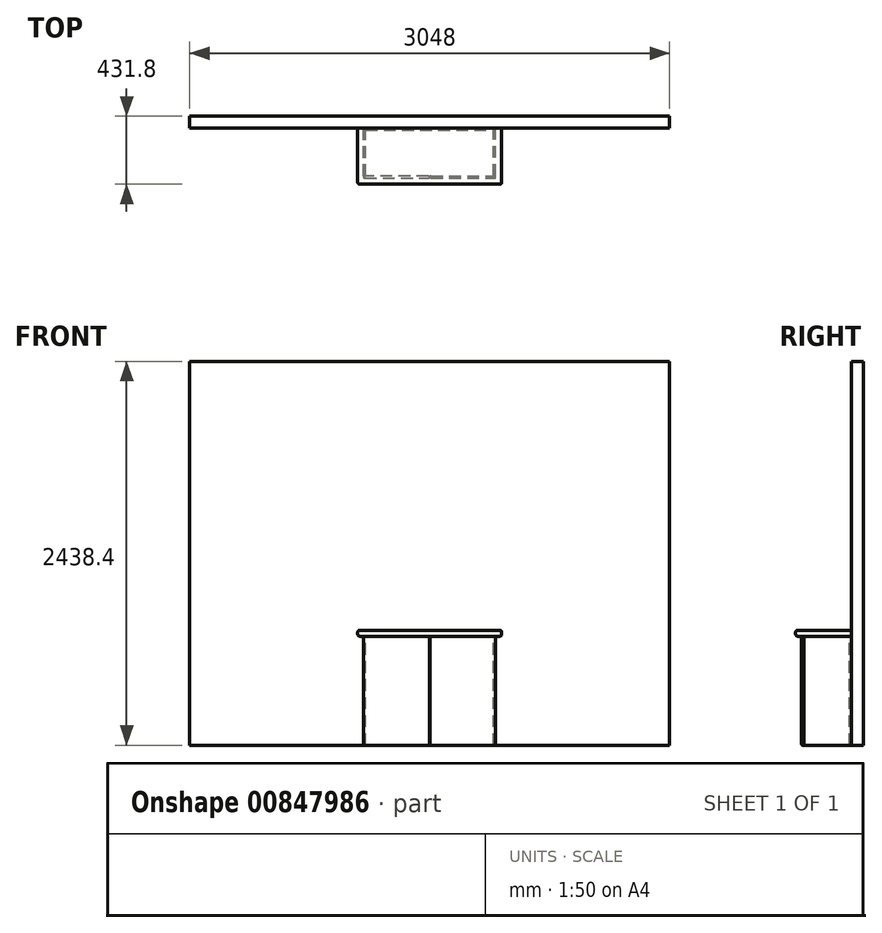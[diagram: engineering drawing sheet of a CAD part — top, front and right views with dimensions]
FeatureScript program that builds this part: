
annotation { "Feature Type Name" : "Feature", "Feature Type Description" : "" }
export const myFeature = defineFeature(function(context is Context, id is Id, definition is map)
    precondition{}
    {
        {
            var Q0;
            Q0=qCreatedBy(makeId("Front.planeOp"),FACE);
            var sketch = newSketch(context, id + "F0", { "sketchPlane" : qUnion([Q0])});
            skLineSegment(sketch, "E0.bottom", {"start": v(1524, -1219.2) * mm, "end": v(-1524, -1219.2) * mm});
            skLineSegment(sketch, "E0.top", {"start": v(1524, 1219.2) * mm, "end": v(-1524, 1219.2) * mm});
            skLineSegment(sketch, "E0.left", {"start": v(1524, -1219.2) * mm, "end": v(1524, 1219.2) * mm});
            skLineSegment(sketch, "E0.right", {"start": v(-1524, -1219.2) * mm, "end": v(-1524, 1219.2) * mm});
            skPoint(sketch, "E0.middle", {"position": v(0, 0) * mm});
            skSolve(sketch);
        }
        {
            var Q0;
            Q0=makeQuery(id+"F0.imprint","IMPRINT",FACE,{"disambiguationData":[TD([[makeQuery(id+"F0.imprint","IMPRINT",EDGE,{"derivedFrom":sQuery(id+"F0.wireOp",EDGE,"E0.bottom")}),-1.0]])]});
            extrude(context, id + "F1", {"entities" : qUnion([Q0]), "depth" : 76.2 * mm, "offsetDistance" : 25.4 * mm});
        }
        {
            var Q0;
            Q0=makeQuery(id+"F1.opExtrude","CAP_FACE",FACE,{"disambiguationData":[OSD([sQuery(id+"F0.wireOp",EDGE,"E0.bottom"),sQuery(id+"F0.wireOp",EDGE,"E0.top"),sQuery(id+"F0.wireOp",EDGE,"E0.left"),sQuery(id+"F0.wireOp",EDGE,"E0.right")])],"isStart":false});
            var sketch = newSketch(context, id + "F2", { "sketchPlane" : qUnion([Q0])});
            skLineSegment(sketch, "E1", {"start": v(0, 1219.2) * mm, "end": v(0, -1219.2) * mm, "construction": true});
            skLineSegment(sketch, "E2", {"start": v(1524, -508) * mm, "end": v(-1524, -508) * mm, "construction": true});
            skLineSegment(sketch, "E3.bottom", {"start": v(457.2, -488.95) * mm, "end": v(-457.2, -488.95) * mm});
            skLineSegment(sketch, "E3.top", {"start": v(457.2, -527.05) * mm, "end": v(-457.2, -527.05) * mm});
            skLineSegment(sketch, "E3.left", {"start": v(457.2, -488.95) * mm, "end": v(457.2, -527.05) * mm});
            skLineSegment(sketch, "E3.right", {"start": v(-457.2, -488.95) * mm, "end": v(-457.2, -527.05) * mm});
            skPoint(sketch, "E3.middle", {"position": v(0, -508) * mm});
            skSolve(sketch);
        }
        {
            var Q0;
            Q0=makeQuery(id+"F2.imprint","IMPRINT",FACE,{"disambiguationData":[TD([[makeQuery(id+"F2.imprint","IMPRINT",EDGE,{"derivedFrom":sQuery(id+"F2.wireOp",EDGE,"E3.bottom")}),1.0]])]});
            extrude(context, id + "F3", {"entities" : qUnion([Q0]), "depth" : 355.6 * mm, "offsetDistance" : 25.4 * mm});
        }
        {
            var Q0;
            Q0=makeQuery(id+"F3.opExtrude","CAP_EDGE",EDGE,{"disambiguationData":[OSD([sQuery(id+"F2.wireOp",EDGE,"E3.left")])],"isStart":false});
            var Q1;
            Q1=makeQuery(id+"F3.opExtrude","CAP_EDGE",EDGE,{"disambiguationData":[OSD([sQuery(id+"F2.wireOp",EDGE,"E3.right")])],"isStart":false});
            fillet(context, id + "F4", {"entities" : qUnion([Q0, Q1]), "radius" : 12.7 * mm, "tangentPropagation" : true, "allowEdgeOverflow" : false});
        }
        {
            var Q0;
            Q0=makeQuery(id+"F3.opExtrude","SWEPT_EDGE",EDGE,{"disambiguationData":[OSD([sQuery(id+"F2.wireOp",EDGE,"E3.bottom"),sQuery(id+"F2.wireOp",EDGE,"E3.left")])]});
            var Q1;
            Q1=makeQuery(id+"F3.opExtrude","SWEPT_EDGE",EDGE,{"disambiguationData":[OSD([sQuery(id+"F2.wireOp",EDGE,"E3.top"),sQuery(id+"F2.wireOp",EDGE,"E3.left")])]});
            var Q2;
            Q2=makeQuery(id+"F3.opExtrude","CAP_EDGE",EDGE,{"disambiguationData":[OSD([sQuery(id+"F2.wireOp",EDGE,"E3.bottom")])],"isStart":false});
            var Q3;
            Q3=makeQuery(id+"F3.opExtrude","CAP_EDGE",EDGE,{"disambiguationData":[OSD([sQuery(id+"F2.wireOp",EDGE,"E3.top")])],"isStart":false});
            var Q4;
            Q4=makeQuery(id+"F3.opExtrude","SWEPT_EDGE",EDGE,{"disambiguationData":[OSD([sQuery(id+"F2.wireOp",EDGE,"E3.bottom"),sQuery(id+"F2.wireOp",EDGE,"E3.right")])]});
            var Q5;
            Q5=makeQuery(id+"F3.opExtrude","SWEPT_EDGE",EDGE,{"disambiguationData":[OSD([sQuery(id+"F2.wireOp",EDGE,"E3.top"),sQuery(id+"F2.wireOp",EDGE,"E3.right")])]});
            fillet(context, id + "F5", {"entities" : qUnion([Q0, Q1, Q2, Q3, Q4, Q5]), "radius" : 12.7 * mm, "tangentPropagation" : true, "allowEdgeOverflow" : false});
        }
        {
            var Q0;
            Q0=makeQuery(id+"F3.opExtrude","SWEPT_FACE",FACE,{"disambiguationData":[OSD([sQuery(id+"F2.wireOp",EDGE,"E3.top")])]});
            var sketch = newSketch(context, id + "F6", { "sketchPlane" : qUnion([Q0])});
            skLineSegment(sketch, "E4.bottom", {"start": v(-406.4, 381) * mm, "end": v(-2.35, 381) * mm});
            skLineSegment(sketch, "E4.top", {"start": v(-419.1, 76.2) * mm, "end": v(419.1, 76.2) * mm});
            skLineSegment(sketch, "E4.left", {"start": v(-419.1, 393.7) * mm, "end": v(-419.1, 381) * mm});
            skLineSegment(sketch, "E4.right", {"start": v(406.4, 378.88) * mm, "end": v(406.4, 88.9) * mm});
            skLineSegment(sketch, "E5.bottom", {"start": v(-419.1, 393.7) * mm, "end": v(-8.7, 393.7) * mm});
            skLineSegment(sketch, "E5.top", {"start": v(-406.4, 88.9) * mm, "end": v(406.4, 88.9) * mm});
            skLineSegment(sketch, "E5.left", {"start": v(-406.4, 379.95) * mm, "end": v(-406.4, 88.9) * mm});
            skLineSegment(sketch, "E5.right", {"start": v(419.1, 387.35) * mm, "end": v(419.1, 381) * mm});
            skLineSegment(sketch, "E6", {"start": v(-406.4, 381) * mm, "end": v(-419.1, 381) * mm});
            skLineSegment(sketch, "E7", {"start": v(406.4, 381) * mm, "end": v(419.1, 381) * mm});
            skLineSegment(sketch, "E8.left", {"start": v(2.35, 387.35) * mm, "end": v(2.35, 381) * mm});
            skLineSegment(sketch, "E8.right", {"start": v(-2.35, 387.35) * mm, "end": v(-2.35, 381) * mm});
            skLineSegment(sketch, "E9.trimOffspring", {"start": v(8.7, 393.7) * mm, "end": v(412.75, 393.7) * mm});
            skLineSegment(sketch, "E10.trimOffspring", {"start": v(2.35, 381) * mm, "end": v(406.4, 381) * mm});
            skLineSegment(sketch, "E11", {"start": v(-419.1, 379.95) * mm, "end": v(-406.4, 379.95) * mm});
            skLineSegment(sketch, "E12", {"start": v(406.4, 378.88) * mm, "end": v(419.1, 378.88) * mm});
            skLineSegment(sketch, "E13.trimOffspring", {"start": v(419.1, 378.88) * mm, "end": v(419.1, 76.2) * mm});
            skLineSegment(sketch, "E14.trimOffspring", {"start": v(-419.1, 379.95) * mm, "end": v(-419.1, 76.2) * mm});
            skPoint(sketch, "E15.visualSharp", {"position": v(-2.35, 393.7) * mm});
            skArc(sketch, "E15.filletArc", {"start": v(-2.35, 387.35) * mm, "mid": v(-4.2, 391.84) * mm, "end": v(-8.7, 393.7) * mm});
            skPoint(sketch, "E16.visualSharp", {"position": v(2.35, 393.7) * mm});
            skArc(sketch, "E16.filletArc", {"start": v(8.7, 393.7) * mm, "mid": v(4.2, 391.84) * mm, "end": v(2.35, 387.35) * mm});
            skPoint(sketch, "E17.visualSharp", {"position": v(419.1, 393.7) * mm});
            skArc(sketch, "E17.filletArc", {"start": v(419.1, 387.35) * mm, "mid": v(417.24, 391.84) * mm, "end": v(412.75, 393.7) * mm});
            skLineSegment(sketch, "E18", {"start": v(-419.1, 381) * mm, "end": v(-419.1, 393.7) * mm});
            skSolve(sketch);
        }
        {
            var Q0;
            Q0=makeQuery(id+"F6.imprint","IMPRINT",FACE,{"disambiguationData":[TD([[makeQuery(id+"F6.imprint","IMPRINT",EDGE,{"derivedFrom":sQuery(id+"F6.wireOp",EDGE,"E4.top")}),-1.0]])]});
            var Q1;
            Q1=makeQuery(id+"F6.imprint","IMPRINT",FACE,{"disambiguationData":[TD([[makeQuery(id+"F6.imprint","IMPRINT",EDGE,{"derivedFrom":sQuery(id+"F6.wireOp",EDGE,"E4.bottom")}),1.0]])]});
            var Q2;
            Q2=makeQuery(id+"F6.imprint","IMPRINT",FACE,{"disambiguationData":[TD([[makeQuery(id+"F6.imprint","IMPRINT",EDGE,{"derivedFrom":sQuery(id+"F6.wireOp",EDGE,"E5.right")}),-1.0]])]});
            var Q3;
            Q3=sQuery(id+"F6.wireOp",EDGE,"E4.left");
            extrude(context, id + "F7", {"entities" : qUnion([Q0, Q1, Q2]), "surfaceEntities" : qUnion([Q3]), "depth" : 692.15 * mm, "offsetDistance" : 25.4 * mm});
        }
        {
            var Q0;
            Q0=makeQuery(id+"F7.opExtrude","CAP_EDGE",EDGE,{"disambiguationData":[OSD([sQuery(id+"F6.wireOp",EDGE,"E9.trimOffspring")])],"isStart":false});
            var Q1;
            Q1=makeQuery(id+"F7.opExtrude","CAP_EDGE",EDGE,{"disambiguationData":[OSD([sQuery(id+"F6.wireOp",EDGE,"E5.bottom")])],"isStart":false});
            var Q2;
            Q2=makeQuery(id+"F7.opExtrude","SWEPT_EDGE",EDGE,{"disambiguationData":[OSD([sQuery(id+"F6.wireOp",EDGE,"E5.bottom"),sQuery(id+"F6.wireOp",EDGE,"E18")])]});
            fillet(context, id + "F8", {"entities" : qUnion([Q0, Q1, Q2]), "radius" : 6.35 * mm, "tangentPropagation" : true, "allowEdgeOverflow" : false});
        }
        {
            var Q0;
            Q0=makeQuery(id+"F7.opExtrude","CAP_EDGE",EDGE,{"disambiguationData":[OSD([sQuery(id+"F6.wireOp",EDGE,"E5.bottom")])],"isStart":true});
            var Q1;
            Q1=makeQuery(id+"F7.opExtrude","CAP_EDGE",EDGE,{"disambiguationData":[OSD([sQuery(id+"F6.wireOp",EDGE,"E9.trimOffspring")])],"isStart":true});
            fillet(context, id + "F9", {"entities" : qUnion([Q0, Q1]), "radius" : 6.35 * mm, "tangentPropagation" : true, "allowEdgeOverflow" : false});
        }
    });
